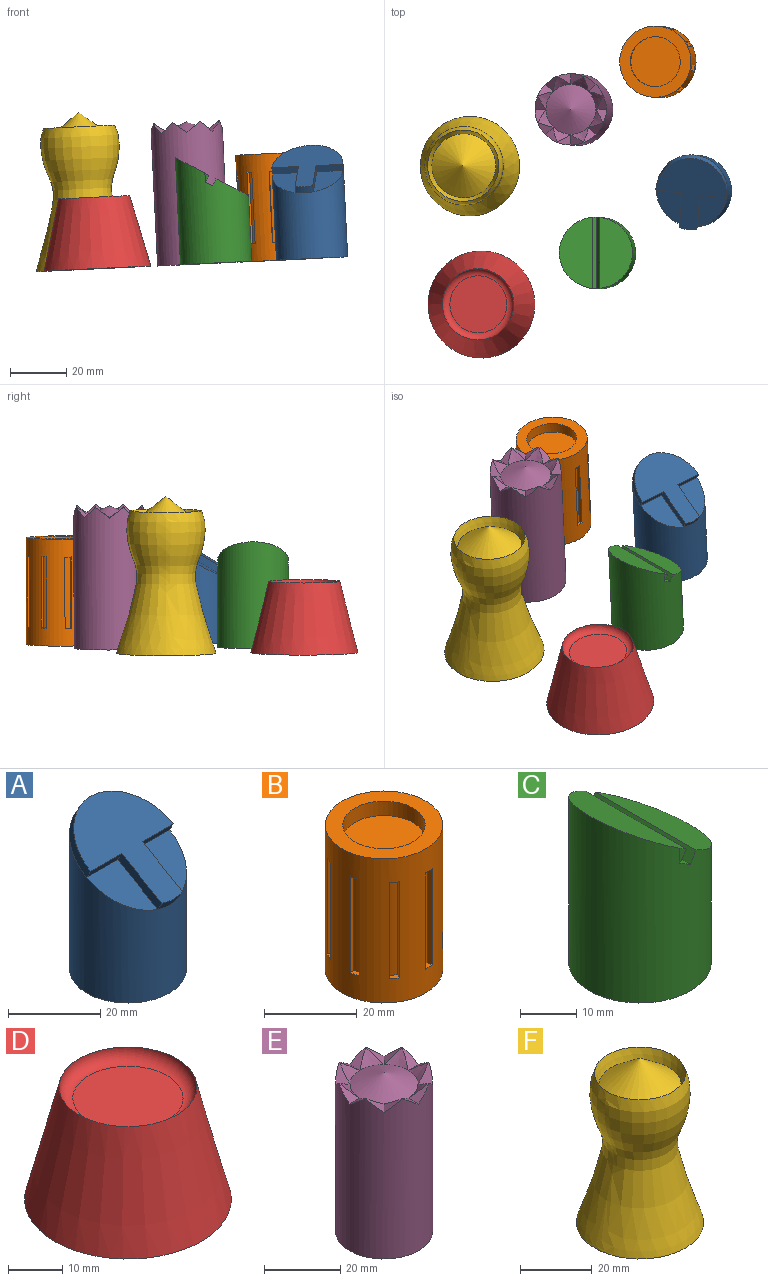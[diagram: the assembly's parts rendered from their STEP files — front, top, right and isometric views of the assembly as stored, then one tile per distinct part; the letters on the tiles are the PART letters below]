
ASSEMBLY  parts=6 mates=5
PART A: 11 faces, bbox 25.4x26.7x40.3 mm
  f0: plane 12.3x9.53mm, normal (0,-0.5,0.87), area 100.2mm2, adj f2,f4,f9
  f1: plane 25.4x25.4mm, normal (0,0,-1), area 506.7mm2, adj f2
  f2: cylinder r=12.7mm len=38.13mm, axis (0,0,1), area 2455.1mm2, adj f0,f1,f3,f5,f8
  f3: plane 12.3x9.53mm, normal (0,-0.5,0.87), area 100.2mm2, adj f2,f6,f7
  f4: plane 9.53x2.2mm, normal (0,-0.87,-0.5), area 24.2mm2, adj f0,f5,f9,f10
  f5: extruded ~25.4x13.97mm, area 109.3mm2, adj f2,f4,f6,f10
  f6: plane 9.53x2.2mm, normal (0,-0.87,-0.5), area 24.2mm2, adj f3,f5,f7,f10
  f7: plane 13.57x9.3mm, normal (-1,0,0), area 36.1mm2, adj f3,f6,f8,f10
  f8: extruded ~6.35x2.43mm, area 16.4mm2, adj f2,f7,f9,f10
  f9: plane 13.57x9.3mm, normal (1,0,0), area 36.1mm2, adj f0,f4,f8,f10
  f10: plane 25.4x25.4mm, normal (0,-0.5,0.87), area 384.7mm2, adj f4,f5,f6,f7,f8,f9
PART B: 50 faces, bbox 25.4x25.4x38.1 mm
  f0: plane 25.4x25.4mm, normal (0,0,1), area 258.4mm2, adj f1,f4
  f1: cylinder r=12.7mm len=38.1mm, axis (0,0,-1), area 2533.5mm2, adj f0,f2,f5,f6,f8,f9,f11,f12
  f2: plane 25.4x25.4mm, normal (0,0,-1), area 506.7mm2, adj f1
  f3: plane 17.78x17.78mm, normal (0,0,1), area 248.3mm2, adj f4
  f4: cylinder r=8.89mm len=17.78mm, axis (0,0,-1), area 212.8mm2, adj f0,f3
  f5: plane 25.4x0.97mm, normal (0.77,0.64,0), area 32.3mm2, adj f1,f7,f8,f9
  f6: plane 25.4x0.97mm, normal (-0.64,-0.77,0), area 32.3mm2, adj f1,f7,f8,f9
  f7: cylinder r=11.43mm len=25.4mm, axis (0,0,-1), area 50.7mm2, adj f5,f6,f8,f9
  f8: plane 2.38x2.38mm, normal (0,0,-1), area 2.7mm2, adj f1,f5,f6,f7
  f9: plane 2.38x2.38mm, normal (0,0,1), area 2.7mm2, adj f1,f5,f6,f7
  f10: cylinder r=11.43mm len=25.4mm, axis (0,0,-1), area 50.7mm2, adj f11,f12,f13,f14
  f11: plane 25.4x1.27mm, normal (1,0,0), area 32.3mm2, adj f1,f10,f13,f14
  f12: plane 25.4x1.25mm, normal (-0.98,-0.17,0), area 32.3mm2, adj f1,f10,f13,f14
  f13: plane 2.21x1.44mm, normal (0,0,-1), area 2.7mm2, adj f1,f10,f11,f12
  f14: plane 2.21x1.44mm, normal (0,0,1), area 2.7mm2, adj f1,f10,f11,f12
  f15: cylinder r=11.43mm len=25.4mm, axis (0,0,-1), area 50.7mm2, adj f16,f17,f18,f19
  f16: plane 25.4x1.25mm, normal (0.17,0.98,0), area 32.3mm2, adj f1,f15,f18,f19
  f17: plane 25.4x1.27mm, normal (0,-1,0), area 32.3mm2, adj f1,f15,f18,f19
  f18: plane 2.21x1.44mm, normal (0,0,-1), area 2.7mm2, adj f1,f15,f16,f17
  f19: plane 2.21x1.44mm, normal (0,0,1), area 2.7mm2, adj f1,f15,f16,f17
  f20: cylinder r=11.43mm len=25.4mm, axis (0,0,-1), area 50.7mm2, adj f21,f22,f23,f24
  f21: plane 25.4x1.1mm, normal (-0.5,0.87,0), area 32.3mm2, adj f1,f20,f23,f24
  f22: plane 25.4x0.97mm, normal (0.64,-0.77,0), area 32.3mm2, adj f1,f20,f23,f24
  f23: plane 2.45x2.24mm, normal (0,0,-1), area 2.7mm2, adj f1,f20,f21,f22
  f24: plane 2.45x2.24mm, normal (0,0,1), area 2.7mm2, adj f1,f20,f21,f22
  f25: cylinder r=11.43mm len=25.4mm, axis (0,0,-1), area 50.7mm2, adj f26,f27,f28,f29
  f26: plane 25.4x1.19mm, normal (-0.94,0.34,0), area 32.3mm2, adj f1,f25,f28,f29
  f27: plane 25.4x1.25mm, normal (0.98,-0.17,0), area 32.3mm2, adj f1,f25,f28,f29
  f28: plane 2.36x1.77mm, normal (0,0,-1), area 2.7mm2, adj f1,f25,f26,f27
  f29: plane 2.36x1.77mm, normal (0,0,1), area 2.7mm2, adj f1,f25,f26,f27
  f30: cylinder r=11.43mm len=25.4mm, axis (0,0,-1), area 50.7mm2, adj f31,f32,f33,f34
  f31: plane 25.4x1.19mm, normal (-0.94,-0.34,0), area 32.3mm2, adj f1,f30,f33,f34
  f32: plane 25.4x1.1mm, normal (0.87,0.5,0), area 32.3mm2, adj f1,f30,f33,f34
  f33: plane 2.44x2.04mm, normal (0,0,-1), area 2.7mm2, adj f1,f30,f31,f32
  f34: plane 2.44x2.04mm, normal (0,0,1), area 2.7mm2, adj f1,f30,f31,f32
  f35: cylinder r=11.43mm len=25.4mm, axis (0,0,-1), area 50.7mm2, adj f36,f37,f38,f39
  f36: plane 25.4x1.1mm, normal (-0.5,-0.87,0), area 32.3mm2, adj f1,f35,f38,f39
  f37: plane 25.4x1.19mm, normal (0.34,0.94,0), area 32.3mm2, adj f1,f35,f38,f39
  f38: plane 2.44x2.04mm, normal (0,0,-1), area 2.7mm2, adj f1,f35,f36,f37
  f39: plane 2.44x2.04mm, normal (0,0,1), area 2.7mm2, adj f1,f35,f36,f37
  f40: cylinder r=11.43mm len=25.4mm, axis (0,0,-1), area 50.7mm2, adj f41,f42,f43,f44
  f41: plane 25.4x1.25mm, normal (0.17,-0.98,0), area 32.3mm2, adj f1,f40,f43,f44
  f42: plane 25.4x1.19mm, normal (-0.34,0.94,0), area 32.3mm2, adj f1,f40,f43,f44
  f43: plane 2.36x1.77mm, normal (0,0,-1), area 2.7mm2, adj f1,f40,f41,f42
  f44: plane 2.36x1.77mm, normal (0,0,1), area 2.7mm2, adj f1,f40,f41,f42
  f45: cylinder r=11.43mm len=25.4mm, axis (0,0,-1), area 50.7mm2, adj f46,f47,f48,f49
  f46: plane 25.4x0.97mm, normal (0.77,-0.64,0), area 32.3mm2, adj f1,f45,f48,f49
  f47: plane 25.4x1.1mm, normal (-0.87,0.5,0), area 32.3mm2, adj f1,f45,f48,f49
  f48: plane 2.45x2.24mm, normal (0,0,-1), area 2.7mm2, adj f1,f45,f46,f47
  f49: plane 2.45x2.24mm, normal (0,0,1), area 2.7mm2, adj f1,f45,f46,f47
PART C: 8 faces, bbox 25.4x25.4x38.1 mm
  f0: cylinder r=12.7mm len=38.11mm, axis (0,0,-1), area 2437.2mm2, adj f1,f2,f3,f4,f5,f6,f7
  f1: cylinder r=12.7mm len=3.23mm, axis (0,0,-1), area 2.3mm2, adj f0,f3,f4
  f2: plane 25.4x25.4mm, normal (0,0,-1), area 506.7mm2, adj f0
  f3: plane 25.32x11.68mm, normal (0.5,0,0.87), area 262.6mm2, adj f0,f1,f4
  f4: plane 25.33x2.43mm, normal (0.87,0,-0.5), area 70.3mm2, adj f0,f1,f3,f5
  f5: plane 25.41x2.43mm, normal (0.5,0,0.87), area 70.5mm2, adj f0,f4,f6
  f6: plane 25.4x2.42mm, normal (-0.87,0,0.5), area 70.8mm2, adj f0,f5,f7
  f7: plane 25.25x11.3mm, normal (0.5,0,0.87), area 251.7mm2, adj f0,f6
PART D: 4 faces, bbox 38.1x38.1x25.4 mm
  f0: cone r=19.05mm half-angle=14deg, axis (0,0,-1), area 2611.5mm2, adj f1,f3
  f1: plane 38.1x38.1mm, normal (0,0,-1), area 1140.1mm2, adj f0
  f2: plane 20.32x20.32mm, normal (0,0,1), area 324.3mm2, adj f3
  f3: torus R=10.16mm, axis (0,0,-1), area 295.2mm2, adj f0,f2
PART E: 27 faces, bbox 25.4x25.4x50.8 mm
  f0: cylinder r=12.7mm len=50.64mm, axis (0,0,-1), area 3897mm2, adj f3,f4,f6,f8,f10,f12,f14,f16
  f1: cone r=12.7mm half-angle=45deg, axis (0,0,1), area 17.9mm2, adj f3,f18,f25
  f2: cone r=12.7mm half-angle=45deg, axis (0,0,1), area 17.9mm2, adj f4,f18,f26
  f3: plane 4.86x3.81mm, normal (-0.6,0,0.8), area 12.3mm2, adj f0,f1,f16,f25
  f4: plane 4.86x3.81mm, normal (0,0.6,0.8), area 12.3mm2, adj f0,f2,f24,f26
  f5: cone r=12.7mm half-angle=45deg, axis (0,0,1), area 17.9mm2, adj f6,f18,f24
  f6: plane 5.45x4.21mm, normal (-0.42,0.42,0.8), area 12.3mm2, adj f0,f5,f23,f24
  f7: cone r=12.7mm half-angle=45deg, axis (0,0,1), area 17.9mm2, adj f8,f18,f23
  f8: plane 4.86x3.81mm, normal (-0.6,0,0.8), area 12.3mm2, adj f0,f7,f22,f23
  f9: cone r=12.7mm half-angle=45deg, axis (0,0,1), area 17.9mm2, adj f10,f18,f22
  f10: plane 5.45x4.21mm, normal (-0.42,-0.42,0.8), area 12.3mm2, adj f0,f9,f21,f22
  f11: cone r=12.7mm half-angle=45deg, axis (0,0,1), area 17.9mm2, adj f12,f18,f21
  f12: plane 4.86x3.81mm, normal (0,-0.6,0.8), area 12.3mm2, adj f0,f11,f20,f21
  f13: cone r=12.7mm half-angle=45deg, axis (0,0,1), area 17.9mm2, adj f14,f18,f20
  f14: plane 5.45x4.21mm, normal (0.42,-0.42,0.8), area 12.3mm2, adj f0,f13,f19,f20
  f15: cone r=12.7mm half-angle=45deg, axis (0,0,1), area 17.9mm2, adj f16,f18,f19
  f16: plane 4.86x3.81mm, normal (0.6,0,0.8), area 12.3mm2, adj f0,f3,f15,f19
  f17: plane 25.4x25.4mm, normal (0,0,-1), area 506.7mm2, adj f0
  f18: cone r=8.89mm half-angle=66.8deg, axis (0,0,-1), area 270.1mm2, adj f1,f2,f5,f7,f9,f11,f13,f15
  f19: plane 5.45x4.21mm, normal (-0.42,0.42,0.8), area 12.3mm2, adj f0,f14,f15,f16
  f20: plane 4.86x3.81mm, normal (0,0.6,0.8), area 12.3mm2, adj f0,f12,f13,f14
  f21: plane 5.45x4.21mm, normal (0.42,0.42,0.8), area 12.3mm2, adj f0,f10,f11,f12
  f22: plane 4.86x3.81mm, normal (0.6,0,0.8), area 12.3mm2, adj f0,f8,f9,f10
  f23: plane 5.45x4.21mm, normal (0.42,-0.42,0.8), area 12.3mm2, adj f0,f6,f7,f8
  f24: plane 4.86x3.81mm, normal (0,-0.6,0.8), area 12.3mm2, adj f0,f4,f5,f6
  f25: plane 5.45x4.21mm, normal (0.42,0.42,0.8), area 12.3mm2, adj f0,f1,f3,f26
  f26: plane 5.45x4.21mm, normal (-0.42,-0.42,0.8), area 12.3mm2, adj f0,f2,f4,f25
PART F: 4 faces, bbox 35.4x35.4x56 mm
  f0: cone r=11.43mm half-angle=18.4deg, axis (0,0,1), area 304.4mm2, adj f1,f3
  f1: revolved ~50.8x35.39mm, area 4348.7mm2, adj f0,f2
  f2: plane 35.39x35.39mm, normal (0,0,-1), area 983.4mm2, adj f1
  f3: cone r=11.43mm half-angle=51.8deg, axis (0,0,-1), area 522.2mm2, adj f0
PLACE A rot(axis=(0.01,-0.36,-0.93),7.5deg) t=(18.55,-15.64,32.92)mm
PLACE B rot(axis=(0,-0.48,-0.88),5.7deg) t=(5.87,30.26,32.24)mm
PLACE C rot(axis=(-0.04,-1,0),2.7deg) t=(-15.63,-37.81,31.33)mm
PLACE D rot(axis=(-0.04,-1,0),2.7deg) t=(-57.86,-56.1,29.34)mm
PLACE E rot(axis=(-0.04,-1,0),2.7deg) t=(-23.78,13.24,30.85)mm
PLACE F rot(axis=(-0.04,-1,0),2.7deg) t=(-61.94,-6.84,29.07)mm
MATE planar F.f0 <-> A.f2  axis (0.05,0,-1) through (-61.94,-6.84,29.07)mm
MATE planar E.f0 <-> A.f2  axis (0.05,0,-1) through (-23.78,13.24,30.85)mm
MATE planar D.f0 <-> C.f0  axis (0.05,0,-1) through (-57.86,-56.1,29.34)mm
MATE planar D.f0 <-> F.f0  axis (0.05,0,-1) through (-57.86,-56.1,29.34)mm
MATE planar A.f2 <-> B.f1  axis (0.05,0,-1) through (18.55,-15.64,32.92)mm
